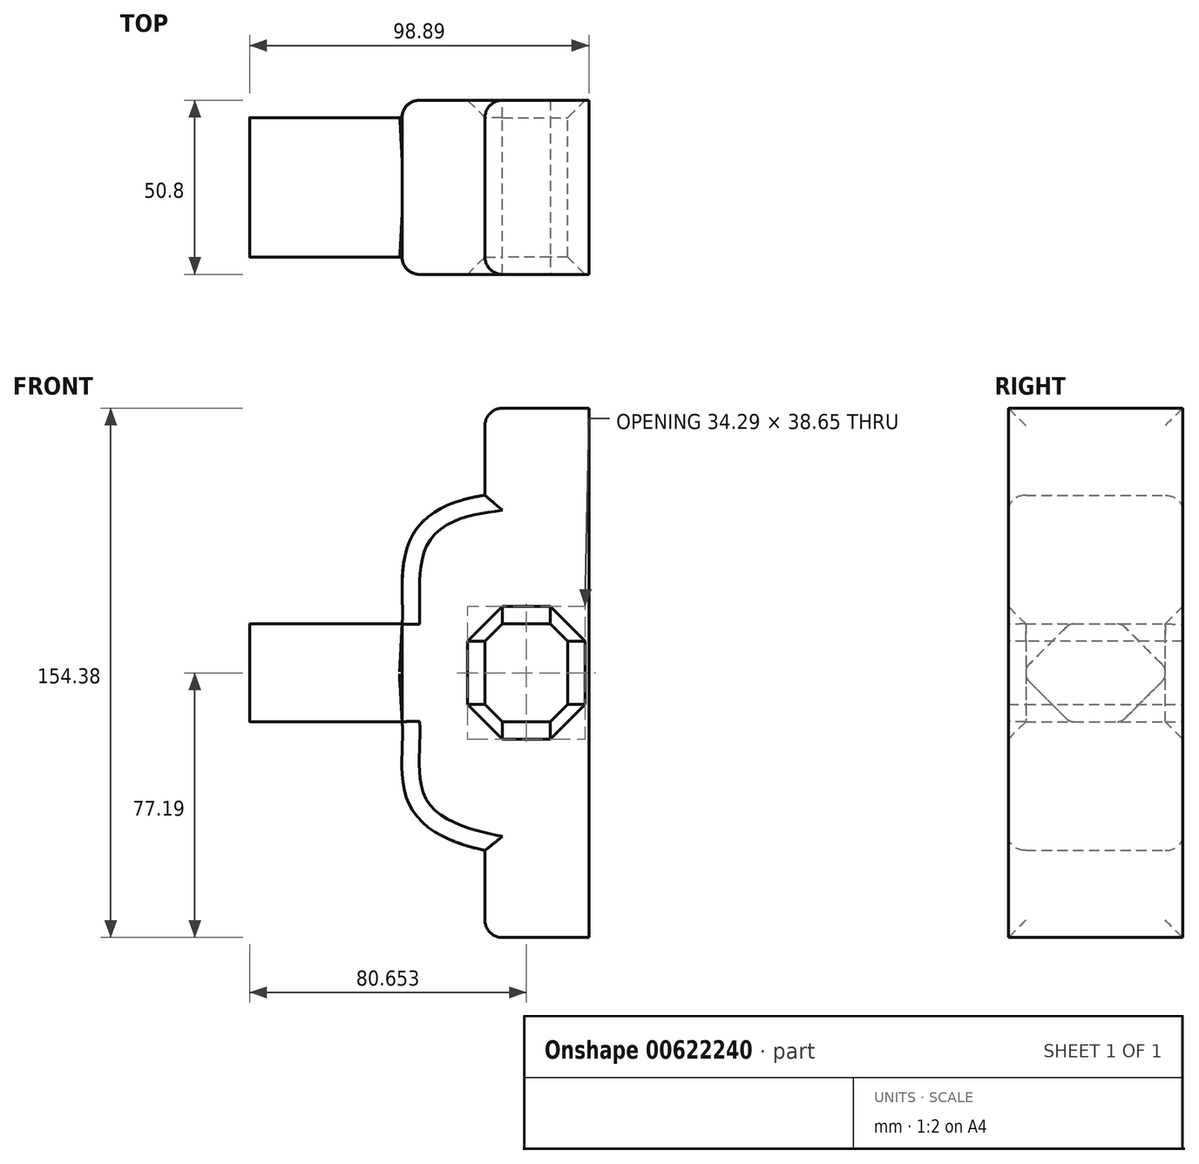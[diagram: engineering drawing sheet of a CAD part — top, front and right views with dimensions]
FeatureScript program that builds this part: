
annotation { "Feature Type Name" : "Feature", "Feature Type Description" : "" }
export const myFeature = defineFeature(function(context is Context, id is Id, definition is map)
    precondition{}
    {
        {
            var Q0;
            Q0=qCreatedBy(makeId("Front.planeOp"),FACE);
            var sketch = newSketch(context, id + "F0", { "sketchPlane" : qUnion([Q0])});
            skLineSegment(sketch, "E0.bottom", {"start": v(15.15, 51.8) * mm, "end": v(-15.15, 51.8) * mm});
            skLineSegment(sketch, "E0.top", {"start": v(15.15, -51.8) * mm, "end": v(-15.15, -51.8) * mm});
            skLineSegment(sketch, "E0.left", {"start": v(15.15, 51.8) * mm, "end": v(15.15, -51.8) * mm});
            skLineSegment(sketch, "E0.right", {"start": v(-15.15, 51.8) * mm, "end": v(-15.15, -51.8) * mm});
            skPoint(sketch, "E0.middle", {"position": v(0, 0) * mm});
            skPoint(sketch, "E1.endSnap0", {"position": v(-15.15, 0) * mm});
            skLineSegment(sketch, "E2.bottom", {"start": v(-39.29, 14.25) * mm, "end": v(8.98, 14.25) * mm});
            skLineSegment(sketch, "E2.top", {"start": v(-39.29, -14.25) * mm, "end": v(8.98, -14.25) * mm});
            skLineSegment(sketch, "E2.left", {"start": v(-39.29, 14.25) * mm, "end": v(-39.29, -14.25) * mm});
            skLineSegment(sketch, "E2.right", {"start": v(8.98, 14.25) * mm, "end": v(8.98, -14.25) * mm});
            skFitSpline(sketch, "E3", {"points": [v(-15.15, 51.8) * mm, v(-39.29, 14.25) * mm], "startDerivative": vector(-87.03, -12.48) * mm, "endDerivative": vector(-2.15, -40.14) * mm});
            skFitSpline(sketch, "E4", {"points": [v(-15.15, -51.8) * mm, v(-39.29, -14.25) * mm], "startDerivative": vector(-89.67, 19.95) * mm, "endDerivative": vector(-2.6, 45.2) * mm});
            skSolve(sketch);
        }
        {
            var Q0;
            Q0 = qSketchRegion(id + "F0", true);
            extrude(context, id + "F1", {"entities" : qUnion([Q0]), "depth" : 50.8 * mm, "offsetDistance" : 25.4 * mm});
        }
        {
            var Q0;
            Q0=makeQuery(id+"F1.opExtrude","SWEPT_FACE",FACE,{"disambiguationData":[OSD([sQuery(id+"F0.wireOp",EDGE,"E0.top")])]});
            var Q1;
            Q1=makeQuery(id+"F1.opExtrude","SWEPT_FACE",FACE,{"disambiguationData":[OSD([sQuery(id+"F0.wireOp",EDGE,"E0.bottom")])]});
            extrude(context, id + "F2", {"entities" : qUnion([Q0, Q1]), "operationType" : NewBodyOperationType.ADD, "depth" : 25.4 * mm, "offsetDistance" : 25.4 * mm});
        }
        {
            var Q0;
            Q0=makeQuery(id+"F1.opExtrude","SWEPT_FACE",FACE,{"disambiguationData":[OSD([sQuery(id+"F0.wireOp",EDGE,"E0.bottom")])]});
            extrude(context, id + "F3", {"entities" : qUnion([Q0]), "operationType" : NewBodyOperationType.ADD, "depth" : 25.4 * mm, "offsetDistance" : 25.4 * mm});
        }
        {
            var Q0;
            Q0=makeQuery(id+"F3.opExtrude","CAP_EDGE",EDGE,{"disambiguationData":[OSD([sQuery(id+"F0.wireOp",EDGE,"E0.bottom"),sQuery(id+"F0.wireOp",EDGE,"E0.right"),sQuery(id+"F0.wireOp",EDGE,"E3")])],"isStart":false});
            var Q1;
            {var subQ0=sQuery(id+"F0.wireOp",EDGE,"E3");var subQ1=sQuery(id+"F0.wireOp",EDGE,"E0.right");var subQ2=sQuery(id+"F0.wireOp",EDGE,"E0.bottom");Q1=makeQuery(id+"F3.opExtrude","SWEPT_EDGE",EDGE,{"disambiguationData":[OSD([subQ2,subQ1,subQ0]),TDD([makeQuery(id+"F1.opExtrude","CAP_VERTEX",VERTEX,{"disambiguationData":[OSD([subQ2,subQ1,subQ0])],"isStart":true})])]});}
            var Q2;
            {var subQ0=sQuery(id+"F0.wireOp",EDGE,"E3");var subQ1=sQuery(id+"F0.wireOp",EDGE,"E0.right");var subQ2=sQuery(id+"F0.wireOp",EDGE,"E0.bottom");Q2=makeQuery(id+"F3.opExtrude","SWEPT_EDGE",EDGE,{"disambiguationData":[OSD([subQ2,subQ1,subQ0]),TDD([makeQuery(id+"F1.opExtrude","CAP_VERTEX",VERTEX,{"disambiguationData":[OSD([subQ2,subQ1,subQ0])],"isStart":false})])]});}
            var Q3;
            {var subQ0=sQuery(id+"F0.wireOp",EDGE,"E4");var subQ1=sQuery(id+"F0.wireOp",EDGE,"E0.right");var subQ2=sQuery(id+"F0.wireOp",EDGE,"E0.top");Q3=makeQuery(id+"F2.opExtrude","SWEPT_EDGE",EDGE,{"disambiguationData":[OSD([subQ2,subQ1,subQ0]),TDD([makeQuery(id+"F1.opExtrude","CAP_VERTEX",VERTEX,{"disambiguationData":[OSD([subQ2,subQ1,subQ0])],"isStart":false})])]});}
            var Q4;
            {var subQ0=sQuery(id+"F0.wireOp",EDGE,"E4");var subQ1=sQuery(id+"F0.wireOp",EDGE,"E0.right");var subQ2=sQuery(id+"F0.wireOp",EDGE,"E0.top");Q4=makeQuery(id+"F2.opExtrude","SWEPT_EDGE",EDGE,{"disambiguationData":[OSD([subQ2,subQ1,subQ0]),TDD([makeQuery(id+"F1.opExtrude","CAP_VERTEX",VERTEX,{"disambiguationData":[OSD([subQ2,subQ1,subQ0])],"isStart":true})])]});}
            var Q5;
            Q5=makeQuery(id+"F2.opExtrude","CAP_EDGE",EDGE,{"disambiguationData":[OSD([sQuery(id+"F0.wireOp",EDGE,"E0.top"),sQuery(id+"F0.wireOp",EDGE,"E0.right"),sQuery(id+"F0.wireOp",EDGE,"E4")])],"isStart":false});
            var Q6;
            Q6=makeQuery(id+"F1.opExtrude","CAP_EDGE",EDGE,{"disambiguationData":[OSD([sQuery(id+"F0.wireOp",EDGE,"E4")])],"isStart":true});
            var Q7;
            Q7=makeQuery(id+"F1.opExtrude","CAP_EDGE",EDGE,{"disambiguationData":[OSD([sQuery(id+"F0.wireOp",EDGE,"E4")])],"isStart":false});
            var Q8;
            Q8=makeQuery(id+"F1.opExtrude","CAP_EDGE",EDGE,{"disambiguationData":[OSD([sQuery(id+"F0.wireOp",EDGE,"E3")])],"isStart":true});
            var Q9;
            Q9=makeQuery(id+"F1.opExtrude","CAP_EDGE",EDGE,{"disambiguationData":[OSD([sQuery(id+"F0.wireOp",EDGE,"E3")])],"isStart":false});
            fillet(context, id + "F4", {"entities" : qUnion([Q0, Q1, Q2, Q3, Q4, Q5, Q6, Q7, Q8, Q9]), "radius" : 5.08 * mm, "tangentPropagation" : true, "allowEdgeOverflow" : false});
        }
        {
            var Q0;
            Q0=makeQuery(id+"F1.opExtrude","CAP_EDGE",EDGE,{"disambiguationData":[OSD([sQuery(id+"F0.wireOp",EDGE,"E2.top")])],"isStart":false});
            var Q1;
            Q1=makeQuery(id+"F1.opExtrude","CAP_EDGE",EDGE,{"disambiguationData":[OSD([sQuery(id+"F0.wireOp",EDGE,"E0.right")])],"isStart":false});
            var Q2;
            Q2=makeQuery(id+"F1.opExtrude","CAP_EDGE",EDGE,{"disambiguationData":[OSD([sQuery(id+"F0.wireOp",EDGE,"E2.bottom")])],"isStart":false});
            var Q3;
            Q3=makeQuery(id+"F1.opExtrude","CAP_EDGE",EDGE,{"disambiguationData":[OSD([sQuery(id+"F0.wireOp",EDGE,"E2.right")])],"isStart":false});
            var Q4;
            Q4=makeQuery(id+"F1.opExtrude","CAP_EDGE",EDGE,{"disambiguationData":[OSD([sQuery(id+"F0.wireOp",EDGE,"E0.right")])],"isStart":true});
            var Q5;
            Q5=makeQuery(id+"F1.opExtrude","CAP_EDGE",EDGE,{"disambiguationData":[OSD([sQuery(id+"F0.wireOp",EDGE,"E2.bottom")])],"isStart":true});
            var Q6;
            Q6=makeQuery(id+"F1.opExtrude","CAP_EDGE",EDGE,{"disambiguationData":[OSD([sQuery(id+"F0.wireOp",EDGE,"E2.right")])],"isStart":true});
            var Q7;
            Q7=makeQuery(id+"F1.opExtrude","CAP_EDGE",EDGE,{"disambiguationData":[OSD([sQuery(id+"F0.wireOp",EDGE,"E2.top")])],"isStart":true});
            var Q8;
            Q8=makeQuery(id+"F1.opExtrude","SWEPT_FACE",FACE,{"disambiguationData":[OSD([sQuery(id+"F0.wireOp",EDGE,"E2.top")])]});
            var Q9;
            Q9=makeQuery(id+"F1.opExtrude","SWEPT_FACE",FACE,{"disambiguationData":[OSD([sQuery(id+"F0.wireOp",EDGE,"E2.bottom")])]});
            chamfer(context, id + "F5", {"entities" : qUnion([Q0, Q1, Q2, Q3, Q4, Q5, Q6, Q7, Q8, Q9]), "width" : 5.08 * mm, "tangentPropagation" : true});
        }
        {
            var Q0;
            Q0=makeQuery(id+"F1.opExtrude","SWEPT_FACE",FACE,{"disambiguationData":[OSD([sQuery(id+"F0.wireOp",EDGE,"E2.left")])]});
            extrude(context, id + "F6", {"entities" : qUnion([Q0]), "operationType" : NewBodyOperationType.ADD, "depth" : 44.45 * mm, "offsetDistance" : 25.4 * mm});
        }
        {
            var Q0;
            {var subQ0=sQuery(id+"F0.wireOp",EDGE,"E4");var subQ1=sQuery(id+"F0.wireOp",EDGE,"E2.left");var subQ2=sQuery(id+"F0.wireOp",EDGE,"E3");Q0=makeQuery(id+"F6.opExtrude","SWEPT_EDGE",EDGE,{"disambiguationData":[OSD([subQ1,subQ2,subQ0]),TDD([makeQuery(id+"F4.opFillet","BLEND_VERTEX",VERTEX,{"blendedFrom":[makeQuery(id+"F1.opExtrude","CAP_EDGE",EDGE,{"disambiguationData":[OSD([subQ2])],"isStart":false}),makeQuery(id+"F1.opExtrude","CAP_EDGE",EDGE,{"disambiguationData":[OSD([subQ0])],"isStart":false}),makeQuery(id+"F1.opExtrude","SWEPT_FACE",FACE,{"disambiguationData":[OSD([subQ1])]}),makeQuery(id+"F1.opExtrude","SWEPT_FACE",FACE,{"disambiguationData":[OSD([subQ0])]})],"blendedInto":[makeQuery(id+"F1.opExtrude","SWEPT_FACE",FACE,{"disambiguationData":[OSD([subQ1])]}),makeQuery(id+"F1.opExtrude","SWEPT_FACE",FACE,{"disambiguationData":[OSD([subQ0])]})]})])]});}
            var Q1;
            Q1=makeQuery(id+"F6.opExtrude","SWEPT_EDGE",EDGE,{"disambiguationData":[OSD([sQuery(id+"F0.wireOp",EDGE,"E2.left"),sQuery(id+"F0.wireOp",EDGE,"E3")])]});
            var Q2;
            Q2=makeQuery(id+"F6.opExtrude","SWEPT_EDGE",EDGE,{"disambiguationData":[OSD([sQuery(id+"F0.wireOp",EDGE,"E2.left"),sQuery(id+"F0.wireOp",EDGE,"E4")])]});
            var Q3;
            {var subQ0=sQuery(id+"F0.wireOp",EDGE,"E3");var subQ1=sQuery(id+"F0.wireOp",EDGE,"E2.left");var subQ2=sQuery(id+"F0.wireOp",EDGE,"E4");Q3=makeQuery(id+"F6.opExtrude","SWEPT_EDGE",EDGE,{"disambiguationData":[OSD([subQ1,subQ0,subQ2]),TDD([makeQuery(id+"F4.opFillet","BLEND_VERTEX",VERTEX,{"blendedFrom":[makeQuery(id+"F1.opExtrude","CAP_EDGE",EDGE,{"disambiguationData":[OSD([subQ0])],"isStart":true}),makeQuery(id+"F1.opExtrude","CAP_EDGE",EDGE,{"disambiguationData":[OSD([subQ2])],"isStart":true}),makeQuery(id+"F1.opExtrude","SWEPT_FACE",FACE,{"disambiguationData":[OSD([subQ1])]}),makeQuery(id+"F1.opExtrude","SWEPT_FACE",FACE,{"disambiguationData":[OSD([subQ0])]})],"blendedInto":[makeQuery(id+"F1.opExtrude","SWEPT_FACE",FACE,{"disambiguationData":[OSD([subQ1])]}),makeQuery(id+"F1.opExtrude","SWEPT_FACE",FACE,{"disambiguationData":[OSD([subQ0])]})]})])]});}
            chamfer(context, id + "F7", {"entities" : qUnion([Q0, Q1, Q2, Q3]), "width" : 12.7 * mm, "tangentPropagation" : true});
        }
        {
            var Q0;
            {var subQ0=sQuery(id+"F0.wireOp",EDGE,"E3");var subQ1=sQuery(id+"F0.wireOp",EDGE,"E2.left");Q0=makeQuery(id+"F7.opChamfer","BLEND_EDGE",EDGE,{"blendedFrom":[makeQuery(id+"F6.opExtrude","SWEPT_EDGE",EDGE,{"disambiguationData":[OSD([subQ1,subQ0])]}),makeQuery(id+"F6.opExtrude","SWEPT_FACE",FACE,{"disambiguationData":[OSD([subQ1,subQ0])]})],"blendedInto":[makeQuery(id+"F6.opExtrude","SWEPT_FACE",FACE,{"disambiguationData":[OSD([subQ1,subQ0])]})]});}
            var Q1;
            {var subQ0=sQuery(id+"F0.wireOp",EDGE,"E3");var subQ1=sQuery(id+"F0.wireOp",EDGE,"E2.left");var subQ2=sQuery(id+"F0.wireOp",EDGE,"E4");Q1=makeQuery(id+"F7.opChamfer","BLEND_EDGE",EDGE,{"blendedFrom":[makeQuery(id+"F6.opExtrude","SWEPT_EDGE",EDGE,{"disambiguationData":[OSD([subQ1,subQ0,subQ2]),TDD([makeQuery(id+"F4.opFillet","BLEND_VERTEX",VERTEX,{"blendedFrom":[makeQuery(id+"F1.opExtrude","CAP_EDGE",EDGE,{"disambiguationData":[OSD([subQ0])],"isStart":false}),makeQuery(id+"F1.opExtrude","CAP_EDGE",EDGE,{"disambiguationData":[OSD([subQ2])],"isStart":false}),makeQuery(id+"F1.opExtrude","SWEPT_FACE",FACE,{"disambiguationData":[OSD([subQ1])]}),makeQuery(id+"F1.opExtrude","SWEPT_FACE",FACE,{"disambiguationData":[OSD([subQ2])]})],"blendedInto":[makeQuery(id+"F1.opExtrude","SWEPT_FACE",FACE,{"disambiguationData":[OSD([subQ1])]}),makeQuery(id+"F1.opExtrude","SWEPT_FACE",FACE,{"disambiguationData":[OSD([subQ2])]})]})])]}),makeQuery(id+"F6.opExtrude","SWEPT_FACE",FACE,{"disambiguationData":[OSD([subQ1,subQ0])]})],"blendedInto":[makeQuery(id+"F6.opExtrude","SWEPT_FACE",FACE,{"disambiguationData":[OSD([subQ1,subQ0])]})]});}
            var Q2;
            {var subQ0=sQuery(id+"F0.wireOp",EDGE,"E4");var subQ1=sQuery(id+"F0.wireOp",EDGE,"E2.left");var subQ2=sQuery(id+"F0.wireOp",EDGE,"E3");Q2=makeQuery(id+"F7.opChamfer","BLEND_EDGE",EDGE,{"blendedFrom":[makeQuery(id+"F6.opExtrude","SWEPT_EDGE",EDGE,{"disambiguationData":[OSD([subQ1,subQ2,subQ0]),TDD([makeQuery(id+"F4.opFillet","BLEND_VERTEX",VERTEX,{"blendedFrom":[makeQuery(id+"F1.opExtrude","CAP_EDGE",EDGE,{"disambiguationData":[OSD([subQ2])],"isStart":true}),makeQuery(id+"F1.opExtrude","CAP_EDGE",EDGE,{"disambiguationData":[OSD([subQ0])],"isStart":true}),makeQuery(id+"F1.opExtrude","SWEPT_FACE",FACE,{"disambiguationData":[OSD([subQ1])]}),makeQuery(id+"F1.opExtrude","SWEPT_FACE",FACE,{"disambiguationData":[OSD([subQ2])]})],"blendedInto":[makeQuery(id+"F1.opExtrude","SWEPT_FACE",FACE,{"disambiguationData":[OSD([subQ1])]}),makeQuery(id+"F1.opExtrude","SWEPT_FACE",FACE,{"disambiguationData":[OSD([subQ2])]})]})])]}),makeQuery(id+"F6.opExtrude","SWEPT_FACE",FACE,{"disambiguationData":[OSD([subQ1,subQ0])]})],"blendedInto":[makeQuery(id+"F6.opExtrude","SWEPT_FACE",FACE,{"disambiguationData":[OSD([subQ1,subQ0])]})]});}
            var Q3;
            {var subQ0=sQuery(id+"F0.wireOp",EDGE,"E4");var subQ1=sQuery(id+"F0.wireOp",EDGE,"E2.left");Q3=makeQuery(id+"F7.opChamfer","BLEND_EDGE",EDGE,{"blendedFrom":[makeQuery(id+"F6.opExtrude","SWEPT_EDGE",EDGE,{"disambiguationData":[OSD([subQ1,subQ0])]}),makeQuery(id+"F6.opExtrude","SWEPT_FACE",FACE,{"disambiguationData":[OSD([subQ1,subQ0])]})],"blendedInto":[makeQuery(id+"F6.opExtrude","SWEPT_FACE",FACE,{"disambiguationData":[OSD([subQ1,subQ0])]})]});}
            var Q4;
            {var subQ0=sQuery(id+"F0.wireOp",EDGE,"E3");var subQ1=sQuery(id+"F0.wireOp",EDGE,"E2.left");var subQ2=sQuery(id+"F0.wireOp",EDGE,"E4");Q4=makeQuery(id+"F7.opChamfer","BLEND_EDGE",EDGE,{"blendedFrom":[makeQuery(id+"F6.opExtrude","SWEPT_EDGE",EDGE,{"disambiguationData":[OSD([subQ1,subQ0,subQ2]),TDD([makeQuery(id+"F4.opFillet","BLEND_VERTEX",VERTEX,{"blendedFrom":[makeQuery(id+"F1.opExtrude","CAP_EDGE",EDGE,{"disambiguationData":[OSD([subQ0])],"isStart":true}),makeQuery(id+"F1.opExtrude","CAP_EDGE",EDGE,{"disambiguationData":[OSD([subQ2])],"isStart":true}),makeQuery(id+"F1.opExtrude","SWEPT_FACE",FACE,{"disambiguationData":[OSD([subQ1])]}),makeQuery(id+"F1.opExtrude","SWEPT_FACE",FACE,{"disambiguationData":[OSD([subQ0])]})],"blendedInto":[makeQuery(id+"F1.opExtrude","SWEPT_FACE",FACE,{"disambiguationData":[OSD([subQ1])]}),makeQuery(id+"F1.opExtrude","SWEPT_FACE",FACE,{"disambiguationData":[OSD([subQ0])]})]})])]}),makeQuery(id+"F6.opExtrude","SWEPT_FACE",FACE,{"disambiguationData":[OSD([sQuery(id+"F0.wireOp",EDGE,"E2.bottom"),subQ1,subQ0])]})],"blendedInto":[makeQuery(id+"F6.opExtrude","SWEPT_FACE",FACE,{"disambiguationData":[OSD([sQuery(id+"F0.wireOp",EDGE,"E2.bottom"),subQ1,subQ0])]})]});}
            var Q5;
            {var subQ0=sQuery(id+"F0.wireOp",EDGE,"E3");var subQ1=sQuery(id+"F0.wireOp",EDGE,"E2.left");Q5=makeQuery(id+"F7.opChamfer","BLEND_EDGE",EDGE,{"blendedFrom":[makeQuery(id+"F6.opExtrude","SWEPT_EDGE",EDGE,{"disambiguationData":[OSD([subQ1,subQ0])]}),makeQuery(id+"F6.opExtrude","SWEPT_FACE",FACE,{"disambiguationData":[OSD([sQuery(id+"F0.wireOp",EDGE,"E2.bottom"),subQ1,subQ0])]})],"blendedInto":[makeQuery(id+"F6.opExtrude","SWEPT_FACE",FACE,{"disambiguationData":[OSD([sQuery(id+"F0.wireOp",EDGE,"E2.bottom"),subQ1,subQ0])]})]});}
            var Q6;
            {var subQ0=sQuery(id+"F0.wireOp",EDGE,"E4");var subQ1=sQuery(id+"F0.wireOp",EDGE,"E2.left");Q6=makeQuery(id+"F7.opChamfer","BLEND_EDGE",EDGE,{"blendedFrom":[makeQuery(id+"F6.opExtrude","SWEPT_EDGE",EDGE,{"disambiguationData":[OSD([subQ1,subQ0])]}),makeQuery(id+"F6.opExtrude","SWEPT_FACE",FACE,{"disambiguationData":[OSD([sQuery(id+"F0.wireOp",EDGE,"E2.top"),subQ1,subQ0])]})],"blendedInto":[makeQuery(id+"F6.opExtrude","SWEPT_FACE",FACE,{"disambiguationData":[OSD([sQuery(id+"F0.wireOp",EDGE,"E2.top"),subQ1,subQ0])]})]});}
            var Q7;
            {var subQ0=sQuery(id+"F0.wireOp",EDGE,"E4");var subQ1=sQuery(id+"F0.wireOp",EDGE,"E2.left");var subQ2=sQuery(id+"F0.wireOp",EDGE,"E3");Q7=makeQuery(id+"F7.opChamfer","BLEND_EDGE",EDGE,{"blendedFrom":[makeQuery(id+"F6.opExtrude","SWEPT_EDGE",EDGE,{"disambiguationData":[OSD([subQ1,subQ2,subQ0]),TDD([makeQuery(id+"F4.opFillet","BLEND_VERTEX",VERTEX,{"blendedFrom":[makeQuery(id+"F1.opExtrude","CAP_EDGE",EDGE,{"disambiguationData":[OSD([subQ2])],"isStart":false}),makeQuery(id+"F1.opExtrude","CAP_EDGE",EDGE,{"disambiguationData":[OSD([subQ0])],"isStart":false}),makeQuery(id+"F1.opExtrude","SWEPT_FACE",FACE,{"disambiguationData":[OSD([subQ1])]}),makeQuery(id+"F1.opExtrude","SWEPT_FACE",FACE,{"disambiguationData":[OSD([subQ0])]})],"blendedInto":[makeQuery(id+"F1.opExtrude","SWEPT_FACE",FACE,{"disambiguationData":[OSD([subQ1])]}),makeQuery(id+"F1.opExtrude","SWEPT_FACE",FACE,{"disambiguationData":[OSD([subQ0])]})]})])]}),makeQuery(id+"F6.opExtrude","SWEPT_FACE",FACE,{"disambiguationData":[OSD([sQuery(id+"F0.wireOp",EDGE,"E2.top"),subQ1,subQ0])]})],"blendedInto":[makeQuery(id+"F6.opExtrude","SWEPT_FACE",FACE,{"disambiguationData":[OSD([sQuery(id+"F0.wireOp",EDGE,"E2.top"),subQ1,subQ0])]})]});}
            fillet(context, id + "F8", {"entities" : qUnion([Q0, Q1, Q2, Q3, Q4, Q5, Q6, Q7]), "radius" : 3.08 * mm, "tangentPropagation" : true, "allowEdgeOverflow" : false});
        }
    });
